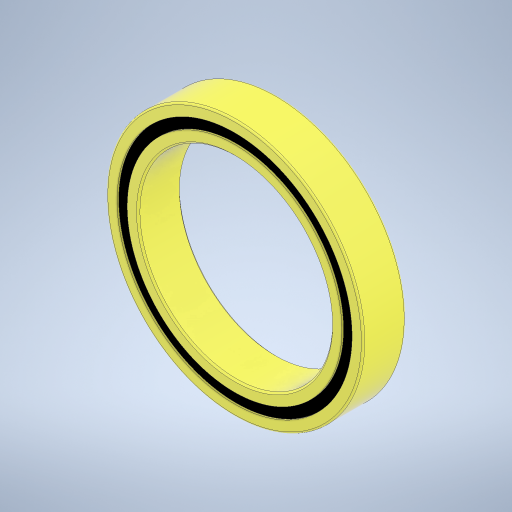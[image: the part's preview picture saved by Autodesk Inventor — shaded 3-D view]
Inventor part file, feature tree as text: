
AUTODESK INVENTOR PART (.ipt)
format: ipt  version: 2024 (Build 280153000, 153)  size: 311,296 bytes
history: native  units: in
note: dims shown in document units (in); Inventor stores cm internally (conversion verified against a paired STEP export)
features: extrude x2, sketch x2, fillet x1, chamfer x1
ambient origin geometry x8: Origin, YZ Plane, XZ Plane, XY Plane, X Axis, Y Axis, Z Axis, Center Point
bodies: Solid1 (feature_tree)
feature tree (6):
  extrude  "Extrusion1"  Depth=0.75in
  fillet  "Fillet1"  Radius=0.032in
  chamfer  "Chamfer1"  Distance=0.125in
  extrude  "Extrusion2"  Depth=0.005in
  sketch  "Sketch1"  dims[d0=0.5625in d1=0.75in d2=0.032in]
  sketch  "Sketch2"  dims[d3=0.032in d4=0.125in d5=0.0in d6=0.005in d7=0.005in d8=0.125in d9=45.0deg d10=0.115in d11=0.0in]
